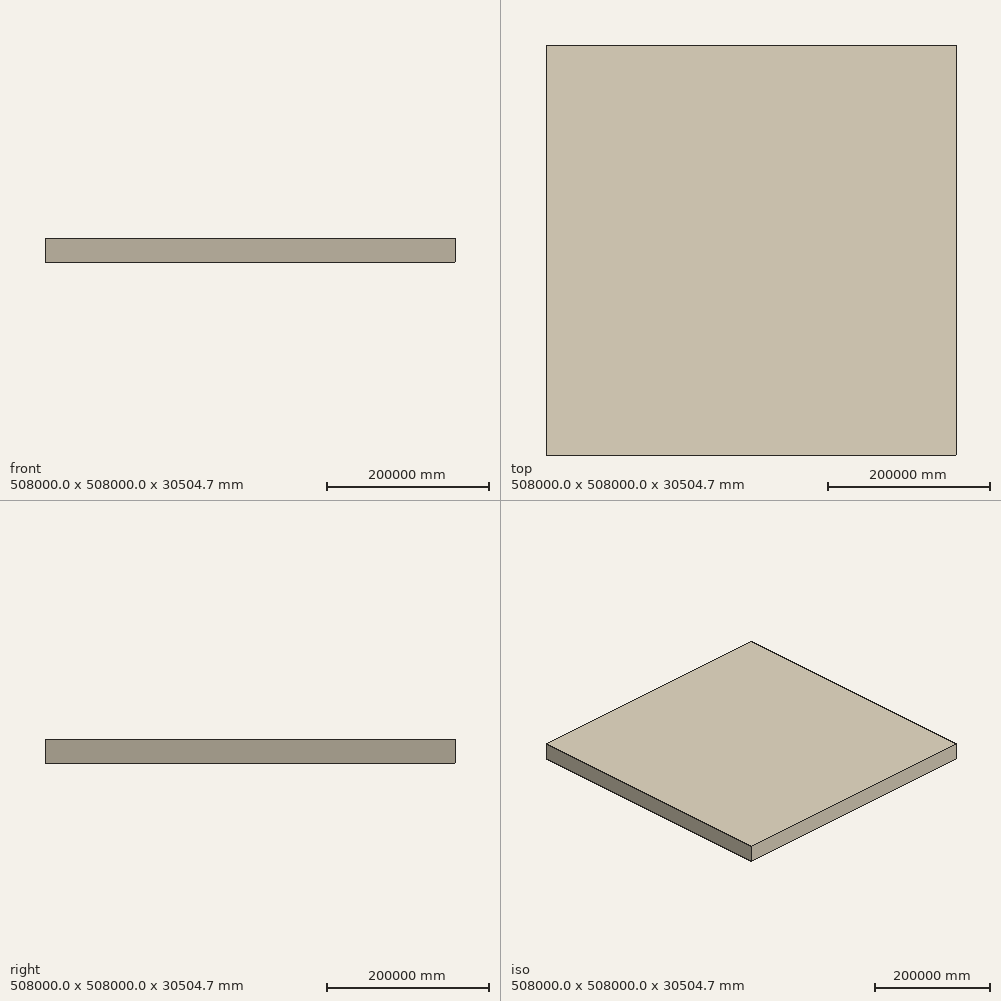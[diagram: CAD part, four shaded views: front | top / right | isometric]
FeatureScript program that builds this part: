
annotation { "Feature Type Name" : "Feature", "Feature Type Description" : "" }
export const myFeature = defineFeature(function(context is Context, id is Id, definition is map)
    precondition{}
    {
        {
            var Q0;
            Q0=qCreatedBy(makeId("Front.planeOp"),FACE);
            var sketch = newSketch(context, id + "F0", { "sketchPlane" : qUnion([Q0])});
            skLineSegment(sketch, "E0", {"start": v(-63.5, 44.66) * mm, "end": v(-26.75, 21.63) * mm});
            skLineSegment(sketch, "E1", {"start": v(-26.75, 21.63) * mm, "end": v(6.28, 40) * mm});
            skLineSegment(sketch, "E2", {"start": v(6.28, 40) * mm, "end": v(41.17, -19.07) * mm});
            skLineSegment(sketch, "E3", {"start": v(41.17, -19.07) * mm, "end": v(-11.63, -24.65) * mm});
            skLineSegment(sketch, "E4", {"start": v(-11.63, -24.65) * mm, "end": v(-26.75, 21.63) * mm});
            skLineSegment(sketch, "E5", {"start": v(-26.75, 21.63) * mm, "end": v(-51.87, 7.9) * mm});
            skLineSegment(sketch, "E6", {"start": v(-51.87, 7.9) * mm, "end": v(-69.31, 21.63) * mm});
            skLineSegment(sketch, "E7", {"start": v(-69.31, 21.63) * mm, "end": v(-63.5, 44.66) * mm});
            skSolve(sketch);
        }
        {
            var Q0;
            Q0=makeQuery(id+"F0.imprint","IMPRINT",FACE,{"disambiguationData":[TD([[makeQuery(id+"F0.imprint","IMPRINT",EDGE,{"derivedFrom":sQuery(id+"F0.wireOp",EDGE,"E0")}),-1.0]])]});
            var Q1;
            Q1=makeQuery(id+"F0.imprint","IMPRINT",FACE,{"disambiguationData":[TD([[makeQuery(id+"F0.imprint","IMPRINT",EDGE,{"derivedFrom":sQuery(id+"F0.wireOp",EDGE,"E1")}),-1.0]])]});
            extrude(context, id + "F1", {"entities" : qUnion([Q0, Q1]), "depth" : 68.33 * mm});
        }
        {
            var Q0;
            Q0=qCreatedBy(makeId("Front.planeOp"),FACE);
            var sketch = newSketch(context, id + "F2", { "sketchPlane" : qUnion([Q0])});
            skCircle(sketch, "E8", {"center": v(44.42, 33.5) * mm, "radius": 33.66 * mm});
            skSolve(sketch);
        }
        {
            var Q0;
            Q0 = qSketchRegion(id + "F2", true);
            extrude(context, id + "F3", {"entities" : qUnion([Q0]), "operationType" : NewBodyOperationType.ADD, "depth" : 128.27 * mm});
        }
        {
            var Q0;
            Q0=makeQuery(id+"F3.opExtrude","CAP_FACE",FACE,{"disambiguationData":[OSD([sQuery(id+"F2.wireOp",EDGE,"E8")])],"isStart":false});
            extrude(context, id + "F4", {"entities" : qUnion([Q0]), "operationType" : NewBodyOperationType.ADD, "oppositeDirection" : true, "depth" : 89.92 * mm});
        }
        {
            var Q0;
            Q0=makeQuery(id+"F3.opExtrude","CAP_FACE",FACE,{"disambiguationData":[OSD([sQuery(id+"F2.wireOp",EDGE,"E8")])],"isStart":false});
            extrude(context, id + "F5", {"entities" : qUnion([Q0]), "operationType" : NewBodyOperationType.ADD, "oppositeDirection" : true, "depth" : 52.83 * mm});
        }
        {
            var Q0;
            Q0=makeQuery(id+"F3.opExtrude","CAP_FACE",FACE,{"disambiguationData":[OSD([sQuery(id+"F2.wireOp",EDGE,"E8")])],"isStart":false});
            extrude(context, id + "F6", {"entities" : qUnion([Q0]), "operationType" : NewBodyOperationType.ADD, "oppositeDirection" : true, "depth" : 89.92 * mm});
        }
        {
            var Q0;
            Q0=makeQuery(id+"F1.opExtrude","CAP_FACE",FACE,{"disambiguationData":[OSD([sQuery(id+"F0.wireOp",EDGE,"E0"),sQuery(id+"F0.wireOp",EDGE,"E5"),sQuery(id+"F0.wireOp",EDGE,"E6"),sQuery(id+"F0.wireOp",EDGE,"E7")])],"isStart":true});
            extrude(context, id + "F7", {"entities" : qUnion([Q0]), "operationType" : NewBodyOperationType.ADD, "depth" : 130.3 * mm});
        }
        {
            var Q0;
            {var subQ0=sQuery(id+"F0.wireOp",EDGE,"E0");Q0=makeQuery(id+"F7.boolean.opBoolean","MERGE",FACE,{"derivedFrom":[makeQuery(id+"F1.opExtrude","SWEPT_FACE",FACE,{"disambiguationData":[OSD([subQ0])]}),makeQuery(id+"F7.opExtrude","SWEPT_FACE",FACE,{"disambiguationData":[OSD([subQ0])]})]});}
            var sketch = newSketch(context, id + "F8", { "sketchPlane" : qUnion([Q0])});
            skLineSegment(sketch, "E9", {"start": v(-34.15, 46.2) * mm, "end": v(-77.52, 30.99) * mm});
            skSolve(sketch);
        }
        {
            var Q0;
            Q0 = qSketchRegion(id + "F8", true);
            var Q1;
            {var subQ0=sQuery(id+"F8.wireOp",EDGE,"E9");Q1=makeQuery(id+"F8.imprint","IMPRINT",FACE,{"disambiguationData":[TD([[makeQuery(id+"F8.imprint","IMPRINT",EDGE,{"derivedFrom":subQ0}),-1.0]])]});}
            extrude(context, id + "F9", {"entities" : qUnion([Q0, Q1]), "operationType" : NewBodyOperationType.ADD, "depth" : 221.74 * mm});
        }
        {
            var Q0;
            Q0=qCreatedBy(makeId("Top.planeOp"),FACE);
            var sketch = newSketch(context, id + "F10", { "sketchPlane" : qUnion([Q0])});
            skLineSegment(sketch, "E10.bottom", {"start": v(-253606.24, 398626.28) * mm, "end": v(254393.76, 398626.28) * mm});
            skLineSegment(sketch, "E10.top", {"start": v(-253606.24, -109373.72) * mm, "end": v(254393.76, -109373.72) * mm});
            skLineSegment(sketch, "E10.left", {"start": v(-253606.24, 398626.28) * mm, "end": v(-253606.24, -109373.72) * mm});
            skLineSegment(sketch, "E10.right", {"start": v(254393.76, 398626.28) * mm, "end": v(254393.76, -109373.72) * mm});
            skSolve(sketch);
        }
        {
            var Q0;
            Q0 = qSketchRegion(id + "F10", true);
            extrude(context, id + "F11", {"entities" : qUnion([Q0]), "depth" : 30480 * mm, "offsetDistance" : 25.4 * mm});
        }
    });
